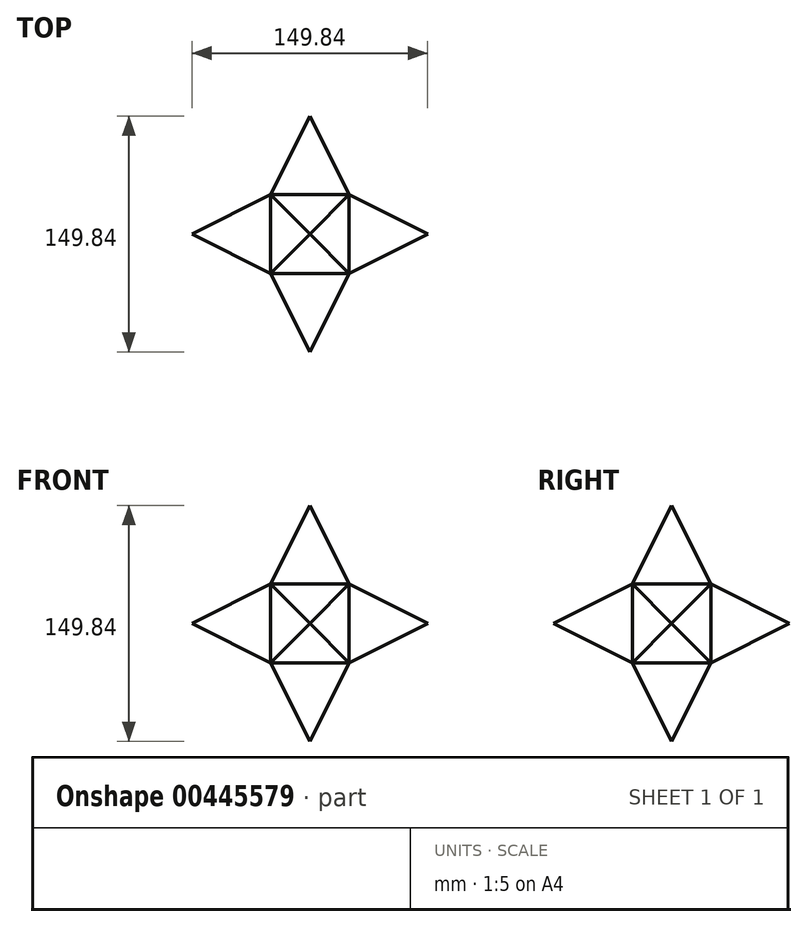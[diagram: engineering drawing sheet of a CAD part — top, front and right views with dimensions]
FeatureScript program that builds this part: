
annotation { "Feature Type Name" : "Feature", "Feature Type Description" : "" }
export const myFeature = defineFeature(function(context is Context, id is Id, definition is map)
    precondition{}
    {
        {
            var Q0;
            Q0=qCreatedBy(makeId("Top.planeOp"),FACE);
            var sketch = newSketch(context, id + "F0", { "sketchPlane" : qUnion([Q0])});
            skLineSegment(sketch, "E0.bottom", {"start": v(-25, -25) * mm, "end": v(25, -25) * mm});
            skLineSegment(sketch, "E0.top", {"start": v(-25, 25) * mm, "end": v(25, 25) * mm});
            skLineSegment(sketch, "E0.left", {"start": v(-25, -25) * mm, "end": v(-25, 25) * mm});
            skLineSegment(sketch, "E0.right", {"start": v(25, -25) * mm, "end": v(25, 25) * mm});
            skPoint(sketch, "E0.middle", {"position": v(0, 0) * mm});
            skSolve(sketch);
        }
        {
            var Q0;
            Q0 = qSketchRegion(id + "F0", true);
            extrude(context, id + "F1", {"entities" : qUnion([Q0]), "endBound" : BoundingType.SYMMETRIC, "depth" : 50 * mm});
        }
        {
            var Q0;
            Q0=makeQuery(id+"F1.opExtrude","CAP_FACE",FACE,{"disambiguationData":[OSD([sQuery(id+"F0.wireOp",EDGE,"E0.bottom"),sQuery(id+"F0.wireOp",EDGE,"E0.top"),sQuery(id+"F0.wireOp",EDGE,"E0.left"),sQuery(id+"F0.wireOp",EDGE,"E0.right")])],"isStart":false});
            var sketch = newSketch(context, id + "F2", { "sketchPlane" : qUnion([Q0])});
            skLineSegment(sketch, "E1.0", {"start": v(-25, -25) * mm, "end": v(-25, 25) * mm});
            skLineSegment(sketch, "E2.0", {"start": v(-25, 25) * mm, "end": v(25, 25) * mm});
            skLineSegment(sketch, "E3.0", {"start": v(-25, -25) * mm, "end": v(25, -25) * mm});
            skLineSegment(sketch, "E4.0", {"start": v(25, -25) * mm, "end": v(25, 25) * mm});
            skSolve(sketch);
        }
        {
            var Q0;
            Q0 = qSketchRegion(id + "F2", true);
            extrude(context, id + "F3", {"entities" : qUnion([Q0]), "depth" : 50 * mm, "hasDraft" : true, "draftAngle" : 26.6 * degree, "draftPullDirection" : true});
        }
        {
            var Q0;
            Q0=makeQuery(id+"F3.opExtrude","SWEPT_BODY",BODY,{"disambiguationData":[OSD([sQuery(id+"F2.wireOp",EDGE,"E1.0"),sQuery(id+"F2.wireOp",EDGE,"E2.0"),sQuery(id+"F2.wireOp",EDGE,"E3.0"),sQuery(id+"F2.wireOp",EDGE,"E4.0")])]});
            var Q1;
            Q1=qCreatedBy(makeId("Top.planeOp"),FACE);
            mirror(context, id + "F4", {"entities" : qUnion([Q0]), "mirrorPlane" : qUnion([Q1])});
        }
        {
            var Q0;
            Q0=makeQuery(id+"F3.opExtrude","CAP_VERTEX",VERTEX,{"disambiguationData":[OSD([sQuery(id+"F2.wireOp",EDGE,"E3.0"),sQuery(id+"F2.wireOp",EDGE,"E4.0")])],"isStart":true});
            var Q1;
            Q1=qCreatedBy(makeId("Origin.pointOp"),VERTEX);
            var Q2;
            Q2=makeQuery(id+"F1.opExtrude","CAP_VERTEX",VERTEX,{"disambiguationData":[OSD([sQuery(id+"F0.wireOp",EDGE,"E0.bottom"),sQuery(id+"F0.wireOp",EDGE,"E0.left")])],"isStart":true});
            cPlane(context, id + "F5", {"entities" : qUnion([Q0, Q1, Q2]), "cplaneType" : CPlaneType.THREE_POINT, "offset" : 25 * mm, "width" : 150 * mm, "height" : 150 * mm});
        }
        {
            var Q0;
            Q0=makeQuery(id+"F3.opExtrude","SWEPT_BODY",BODY,{"disambiguationData":[OSD([sQuery(id+"F2.wireOp",EDGE,"E1.0"),sQuery(id+"F2.wireOp",EDGE,"E2.0"),sQuery(id+"F2.wireOp",EDGE,"E3.0"),sQuery(id+"F2.wireOp",EDGE,"E4.0")])]});
            var Q1;
            Q1=qCreatedBy(id+"F5.planeOp",FACE);
            mirror(context, id + "F6", {"entities" : qUnion([Q0]), "mirrorPlane" : qUnion([Q1])});
        }
        {
            var Q0;
            Q0=makeQuery(id+"F4.opPattern","COPY",BODY,{"derivedFrom":makeQuery(id+"F3.opExtrude","SWEPT_BODY",BODY,{"disambiguationData":[OSD([sQuery(id+"F2.wireOp",EDGE,"E1.0"),sQuery(id+"F2.wireOp",EDGE,"E2.0"),sQuery(id+"F2.wireOp",EDGE,"E3.0"),sQuery(id+"F2.wireOp",EDGE,"E4.0")])]}),"instanceName":"1"});
            var Q1;
            Q1=qCreatedBy(id+"F5.planeOp",FACE);
            mirror(context, id + "F7", {"entities" : qUnion([Q0]), "mirrorPlane" : qUnion([Q1])});
        }
        {
            var Q0;
            Q0=makeQuery(id+"F3.opExtrude","CAP_VERTEX",VERTEX,{"disambiguationData":[OSD([sQuery(id+"F2.wireOp",EDGE,"E2.0"),sQuery(id+"F2.wireOp",EDGE,"E4.0")])],"isStart":true});
            var Q1;
            Q1=qCreatedBy(makeId("Origin.pointOp"),VERTEX);
            var Q2;
            Q2=makeQuery(id+"F3.opExtrude","CAP_VERTEX",VERTEX,{"disambiguationData":[OSD([sQuery(id+"F2.wireOp",EDGE,"E1.0"),sQuery(id+"F2.wireOp",EDGE,"E3.0")])],"isStart":true});
            cPlane(context, id + "F8", {"entities" : qUnion([Q0, Q1, Q2]), "cplaneType" : CPlaneType.THREE_POINT, "offset" : 25 * mm, "width" : 150 * mm, "height" : 150 * mm});
        }
        {
            var Q0;
            Q0=makeQuery(id+"F6.opPattern","COPY",BODY,{"derivedFrom":makeQuery(id+"F3.opExtrude","SWEPT_BODY",BODY,{"disambiguationData":[OSD([sQuery(id+"F2.wireOp",EDGE,"E1.0"),sQuery(id+"F2.wireOp",EDGE,"E2.0"),sQuery(id+"F2.wireOp",EDGE,"E3.0"),sQuery(id+"F2.wireOp",EDGE,"E4.0")])]}),"instanceName":"1"});
            var Q1;
            Q1=qCreatedBy(id+"F8.planeOp",FACE);
            mirror(context, id + "F9", {"entities" : qUnion([Q0]), "mirrorPlane" : qUnion([Q1])});
        }
        {
            var Q0;
            Q0=makeQuery(id+"F7.opPattern","COPY",BODY,{"derivedFrom":makeQuery(id+"F4.opPattern","COPY",BODY,{"derivedFrom":makeQuery(id+"F3.opExtrude","SWEPT_BODY",BODY,{"disambiguationData":[OSD([sQuery(id+"F2.wireOp",EDGE,"E1.0"),sQuery(id+"F2.wireOp",EDGE,"E2.0"),sQuery(id+"F2.wireOp",EDGE,"E3.0"),sQuery(id+"F2.wireOp",EDGE,"E4.0")])]}),"instanceName":"1"}),"instanceName":"1"});
            var Q1;
            Q1=qCreatedBy(id+"F8.planeOp",FACE);
            mirror(context, id + "F10", {"operationType" : NewBodyOperationType.ADD, "entities" : qUnion([Q0]), "mirrorPlane" : qUnion([Q1])});
        }
    });
